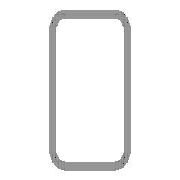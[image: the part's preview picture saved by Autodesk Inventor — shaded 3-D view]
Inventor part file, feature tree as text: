
AUTODESK INVENTOR PART (.ipt)
format: ipt  version: 2025.3 (Build 293356030, 356C)  size: 134,144 bytes
history: native  units: mm (DEFAULTED — no unit token found)
features: other x4, sketch x1, plane x1
ambient origin geometry x8: Origin, YZ Plane, XZ Plane, XY Plane, X Axis, Y Axis, Z Axis, Center Point
bodies: Solid1 (feature_tree), Body (feature_tree)
feature tree (6):
  parser-record x1  (decoder bookkeeping rows leaked as tree rows — omitted from the tree; the rows remain in map.json)
  other  "Driven Length"
  other  "Start Plane"
  other  "End Plane"
  sketch  "Sketch3"  dims[d3=360.0mm d4=0.0mm d7=4.0mm d9=20.0mm d11=40.0mm d12=2.0mm d13=-0.0mm d14=360.0mm d15=10.0mm d16=20.0mm d17=90.0deg d18=360.0mm]
  plane  "Work Plane3"
